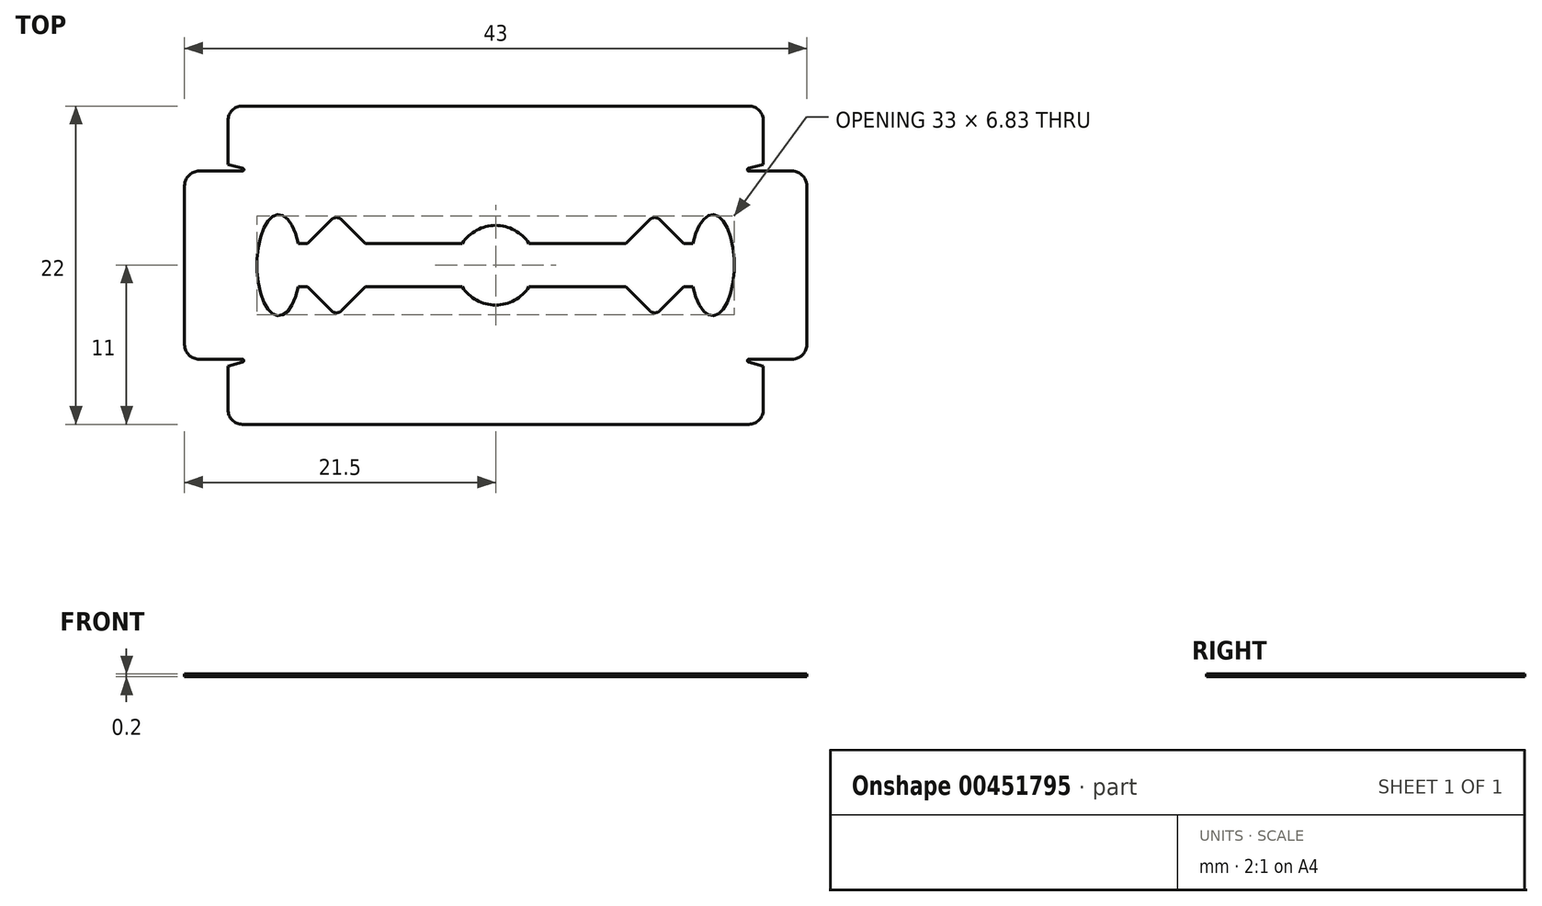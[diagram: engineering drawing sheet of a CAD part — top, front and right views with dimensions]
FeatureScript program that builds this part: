
annotation { "Feature Type Name" : "Feature", "Feature Type Description" : "" }
export const myFeature = defineFeature(function(context is Context, id is Id, definition is map)
    precondition{}
    {
        {
            var Q0;
            Q0=qCreatedBy(makeId("Top.planeOp"),FACE);
            var sketch = newSketch(context, id + "F0", { "sketchPlane" : qUnion([Q0])});
            skLineSegment(sketch, "E0.bottom", {"start": v(18.5, 11) * mm, "end": v(-18.5, 11) * mm});
            skLineSegment(sketch, "E0.top", {"start": v(18.5, -11) * mm, "end": v(-18.5, -11) * mm});
            skLineSegment(sketch, "E0.left", {"start": v(21.5, 6.5) * mm, "end": v(21.5, -6.5) * mm});
            skLineSegment(sketch, "E0.right", {"start": v(-21.5, 6.5) * mm, "end": v(-21.5, -6.5) * mm});
            skPoint(sketch, "E0.middle", {"position": v(0, 0) * mm});
            skLineSegment(sketch, "E1.top", {"start": v(-21.5, -6.5) * mm, "end": v(-18.5, -6.5) * mm});
            skLineSegment(sketch, "E1.right", {"start": v(-18.5, -11) * mm, "end": v(-18.5, -6.5) * mm});
            skLineSegment(sketch, "E2.top", {"start": v(-21.5, 6.5) * mm, "end": v(-18.5, 6.5) * mm});
            skLineSegment(sketch, "E2.right", {"start": v(-18.5, 11) * mm, "end": v(-18.5, 6.5) * mm});
            skLineSegment(sketch, "E3.top", {"start": v(21.5, -6.5) * mm, "end": v(18.5, -6.5) * mm});
            skLineSegment(sketch, "E3.right", {"start": v(18.5, -11) * mm, "end": v(18.5, -6.5) * mm});
            skLineSegment(sketch, "E4.top", {"start": v(21.5, 6.5) * mm, "end": v(18.5, 6.5) * mm});
            skLineSegment(sketch, "E4.right", {"start": v(18.5, 11) * mm, "end": v(18.5, 6.5) * mm});
            skCircle(sketch, "E5", {"center": v(0, 0) * mm, "radius": 2.5 * mm});
            skSolve(sketch);
        }
        {
            var Q0;
            Q0=qCreatedBy(makeId("Top.planeOp"),FACE);
            var sketch = newSketch(context, id + "F1", { "sketchPlane" : qUnion([Q0])});
            skLineSegment(sketch, "E6.bottom", {"start": v(17.5, 11) * mm, "end": v(-17.5, 11) * mm});
            skLineSegment(sketch, "E6.top", {"start": v(17.5, -11) * mm, "end": v(-17.5, -11) * mm});
            skLineSegment(sketch, "E6.left", {"start": v(21.5, 5.5) * mm, "end": v(21.5, -5.5) * mm});
            skLineSegment(sketch, "E6.right", {"start": v(-21.5, 5.5) * mm, "end": v(-21.5, -5.5) * mm});
            skPoint(sketch, "E6.middle", {"position": v(0, 0) * mm});
            skLineSegment(sketch, "E7.top", {"start": v(-20.5, -6.5) * mm, "end": v(-18.5, -6.5) * mm});
            skLineSegment(sketch, "E7.right", {"start": v(-18.5, -10) * mm, "end": v(-18.5, -6.97) * mm});
            skLineSegment(sketch, "E8.top", {"start": v(-20.5, 6.5) * mm, "end": v(-18.5, 6.5) * mm});
            skLineSegment(sketch, "E8.right", {"start": v(-18.5, 10) * mm, "end": v(-18.5, 6.97) * mm});
            skLineSegment(sketch, "E9.top", {"start": v(20.5, -6.5) * mm, "end": v(18.5, -6.5) * mm});
            skLineSegment(sketch, "E9.right", {"start": v(18.5, -10) * mm, "end": v(18.5, -6.97) * mm});
            skLineSegment(sketch, "E10.top", {"start": v(20.5, 6.5) * mm, "end": v(18.5, 6.5) * mm});
            skLineSegment(sketch, "E10.right", {"start": v(18.5, 10) * mm, "end": v(18.5, 6.97) * mm});
            skCircle(sketch, "E11", {"center": v(0, 0) * mm, "radius": 2.75 * mm});
            skLineSegment(sketch, "E12", {"start": v(-2.3, 1.5) * mm, "end": v(-7.9, 1.5) * mm});
            skLineSegment(sketch, "E13", {"start": v(-9, 1.5) * mm, "end": v(-10.65, 3.15) * mm});
            skLineSegment(sketch, "E14", {"start": v(-11.35, 3.15) * mm, "end": v(-13, 1.5) * mm});
            skLineSegment(sketch, "E15", {"start": v(-13, 1.5) * mm, "end": v(-13.64, 1.5) * mm});
            skLineSegment(sketch, "E16", {"start": v(-7.9, -1.5) * mm, "end": v(-7.9, -1.5) * mm});
            skEllipticalArc(sketch, "E17", {});
            skPoint(sketch, "E17.centerSnap0", {"position": v(-6, 0) * mm});
            skLineSegment(sketch, "E18", {"start": v(0, 0) * mm, "end": v(-117.9, 0) * mm, "construction": true});
            skLineSegment(sketch, "E19.MirrorCS", {"start": v(-2.3, -1.5) * mm, "end": v(-7.9, -1.5) * mm});
            skLineSegment(sketch, "E20.MirrorCS", {"start": v(-9, -1.5) * mm, "end": v(-10.65, -3.15) * mm});
            skLineSegment(sketch, "E21.MirrorCS", {"start": v(-11.35, -3.15) * mm, "end": v(-13, -1.5) * mm});
            skLineSegment(sketch, "E22.MirrorCS", {"start": v(-13, -1.5) * mm, "end": v(-13.64, -1.5) * mm});
            skPoint(sketch, "E23.visualSharp", {"position": v(-11, 3.5) * mm});
            skArc(sketch, "E23.filletArc", {"start": v(-10.65, 3.15) * mm, "mid": v(-11, 3.3) * mm, "end": v(-11.35, 3.15) * mm});
            skPoint(sketch, "E24.visualSharp", {"position": v(-11, -3.5) * mm});
            skArc(sketch, "E24.filletArc", {"start": v(-11.35, -3.15) * mm, "mid": v(-11, -3.3) * mm, "end": v(-10.65, -3.15) * mm});
            skPoint(sketch, "E25.orphan", {"position": v(-15, 1.5) * mm});
            skPoint(sketch, "E26.orphan", {"position": v(-15, -1.5) * mm});
            skLineSegment(sketch, "E27.trimOffspring", {"start": v(-7.9, 1.5) * mm, "end": v(-7.9, 1.5) * mm});
            skLineSegment(sketch, "E28.trimOffspring", {"start": v(-7.9, 1.5) * mm, "end": v(-9, 1.5) * mm});
            skLineSegment(sketch, "E29.trimOffspring", {"start": v(-7.9, -1.5) * mm, "end": v(-9, -1.5) * mm});
            skPoint(sketch, "E30.visualSharp", {"position": v(-21.5, 6.5) * mm});
            skArc(sketch, "E30.filletArc", {"start": v(-20.5, 6.5) * mm, "mid": v(-21.2, 6.2) * mm, "end": v(-21.5, 5.5) * mm});
            skPoint(sketch, "E31.visualSharp", {"position": v(-21.5, -6.5) * mm});
            skArc(sketch, "E31.filletArc", {"start": v(-21.5, -5.5) * mm, "mid": v(-21.2, -6.2) * mm, "end": v(-20.5, -6.5) * mm});
            skPoint(sketch, "E32.visualSharp", {"position": v(-18.5, 11) * mm});
            skArc(sketch, "E32.filletArc", {"start": v(-17.5, 11) * mm, "mid": v(-18.2, 10.7) * mm, "end": v(-18.5, 10) * mm});
            skPoint(sketch, "E33.visualSharp", {"position": v(-18.5, -11) * mm});
            skArc(sketch, "E33.filletArc", {"start": v(-18.5, -10) * mm, "mid": v(-18.2, -10.7) * mm, "end": v(-17.5, -11) * mm});
            skPoint(sketch, "E34.visualSharp", {"position": v(18.5, 11) * mm});
            skArc(sketch, "E34.filletArc", {"start": v(18.5, 10) * mm, "mid": v(18.2, 10.7) * mm, "end": v(17.5, 11) * mm});
            skPoint(sketch, "E35.visualSharp", {"position": v(21.5, 6.5) * mm});
            skArc(sketch, "E35.filletArc", {"start": v(21.5, 5.5) * mm, "mid": v(21.2, 6.2) * mm, "end": v(20.5, 6.5) * mm});
            skPoint(sketch, "E36.visualSharp", {"position": v(21.5, -6.5) * mm});
            skArc(sketch, "E36.filletArc", {"start": v(20.5, -6.5) * mm, "mid": v(21.2, -6.2) * mm, "end": v(21.5, -5.5) * mm});
            skPoint(sketch, "E37.visualSharp", {"position": v(18.5, -11) * mm});
            skArc(sketch, "E37.filletArc", {"start": v(17.5, -11) * mm, "mid": v(18.2, -10.7) * mm, "end": v(18.5, -10) * mm});
            skLineSegment(sketch, "E38", {"start": v(-18.5, -6.5) * mm, "end": v(-17.5, -6.5) * mm});
            skLineSegment(sketch, "E39", {"start": v(-17.47, -6.7) * mm, "end": v(-18.5, -6.97) * mm});
            skPoint(sketch, "E40.visualSharp", {"position": v(-16.74, -6.5) * mm});
            skArc(sketch, "E40.filletArc", {"start": v(-17.47, -6.7) * mm, "mid": v(-17.4, -6.59) * mm, "end": v(-17.5, -6.5) * mm});
            skLineSegment(sketch, "E41.MirrorCS", {"start": v(-17.47, 6.7) * mm, "end": v(-18.5, 6.97) * mm});
            skLineSegment(sketch, "E42.MirrorCS", {"start": v(-18.5, 6.5) * mm, "end": v(-17.5, 6.5) * mm});
            skArc(sketch, "E43.MirrorCS", {"start": v(-17.47, 6.7) * mm, "mid": v(-17.4, 6.59) * mm, "end": v(-17.5, 6.5) * mm});
            skLineSegment(sketch, "E44", {"start": v(0, -44.64) * mm, "end": v(0, 0) * mm, "construction": true});
            skLineSegment(sketch, "E45.MirrorCS", {"start": v(2.3, 1.5) * mm, "end": v(7.9, 1.5) * mm});
            skLineSegment(sketch, "E46.MirrorCS", {"start": v(2.3, -1.5) * mm, "end": v(7.9, -1.5) * mm});
            skLineSegment(sketch, "E47.MirrorCS", {"start": v(7.9, -1.5) * mm, "end": v(7.9, -1.5) * mm});
            skLineSegment(sketch, "E48.MirrorCS", {"start": v(7.9, 1.5) * mm, "end": v(7.9, 1.5) * mm});
            skLineSegment(sketch, "E49.MirrorCS", {"start": v(7.9, 1.5) * mm, "end": v(9, 1.5) * mm});
            skLineSegment(sketch, "E50.MirrorCS", {"start": v(7.9, -1.5) * mm, "end": v(9, -1.5) * mm});
            skLineSegment(sketch, "E51.MirrorCS", {"start": v(9, -1.5) * mm, "end": v(10.65, -3.15) * mm});
            skArc(sketch, "E52.MirrorCS", {"start": v(11.35, -3.15) * mm, "mid": v(11, -3.3) * mm, "end": v(10.65, -3.15) * mm});
            skLineSegment(sketch, "E53.MirrorCS", {"start": v(11.35, -3.15) * mm, "end": v(13, -1.5) * mm});
            skLineSegment(sketch, "E54.MirrorCS", {"start": v(13, -1.5) * mm, "end": v(13.64, -1.5) * mm});
            skEllipticalArc(sketch, "E55.MirrorCS", {});
            skLineSegment(sketch, "E56.MirrorCS", {"start": v(13, 1.5) * mm, "end": v(13.64, 1.5) * mm});
            skLineSegment(sketch, "E57.MirrorCS", {"start": v(11.35, 3.15) * mm, "end": v(13, 1.5) * mm});
            skArc(sketch, "E58.MirrorCS", {"start": v(10.65, 3.15) * mm, "mid": v(11, 3.3) * mm, "end": v(11.35, 3.15) * mm});
            skLineSegment(sketch, "E59.MirrorCS", {"start": v(9, 1.5) * mm, "end": v(10.65, 3.15) * mm});
            skLineSegment(sketch, "E60.MirrorCS", {"start": v(17.47, -6.7) * mm, "end": v(18.5, -6.97) * mm});
            skLineSegment(sketch, "E61.MirrorCS", {"start": v(18.5, -6.5) * mm, "end": v(17.5, -6.5) * mm});
            skArc(sketch, "E62.MirrorCS", {"start": v(17.47, -6.7) * mm, "mid": v(17.4, -6.59) * mm, "end": v(17.5, -6.5) * mm});
            skLineSegment(sketch, "E63.MirrorCS", {"start": v(17.47, 6.7) * mm, "end": v(18.5, 6.97) * mm});
            skLineSegment(sketch, "E64.MirrorCS", {"start": v(18.5, 6.5) * mm, "end": v(17.5, 6.5) * mm});
            skArc(sketch, "E65.MirrorCS", {"start": v(17.47, 6.7) * mm, "mid": v(17.4, 6.59) * mm, "end": v(17.5, 6.5) * mm});
            const initialGuessF1  = {"E17": [-0.015, 0, 0, 1, 0.0035, 0.0015, 5.1553000244583265, 4.269477936311052], "E55.MirrorCS": [0.015, 0, 0, 1, 0.0035, 0.0015, 2.013707370868533, 1.12788528272126]};
            skSetInitialGuess(sketch, initialGuessF1);
            skSolve(sketch);
        }
        {
            var Q0;
            Q0=qSketchRegion(id+"F1",true);
            extrude(context, id + "F2", {"entities" : qUnion([Q0]), "depth" : 0.2 * mm});
        }
    });
